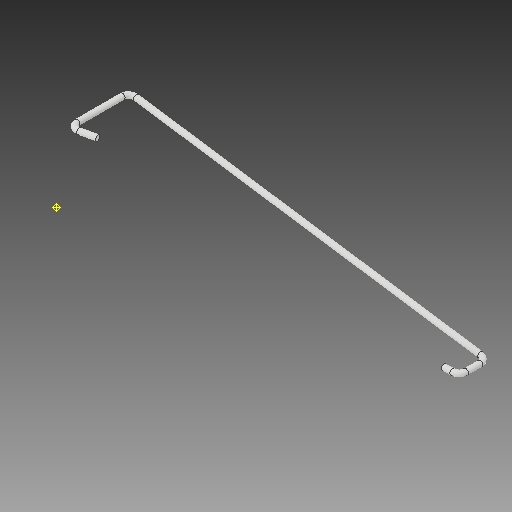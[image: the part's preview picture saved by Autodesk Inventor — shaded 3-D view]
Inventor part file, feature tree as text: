
AUTODESK INVENTOR PART (.ipt)
format: ipt  version: 2017 (Build 210142000, 142)  size: 92,160 bytes
history: native  units: in
note: dims shown in document units (in); Inventor stores cm internally (conversion verified against a paired STEP export)
features: other x4, sketch x1
ambient origin geometry x8: Origin, YZ Plane, XZ Plane, XY Plane, X Axis, Y Axis, Z Axis, Center Point
bodies: Solid1 (feature_tree)
feature tree (5):
  other  "WIRE.ipt"
  other  "Solid1::WIRE.ipt"
  other  "TaggingFeature1"
  sketch  "Sketch1"  dims[d0=0.3937in]
  other  "Work Point1"
